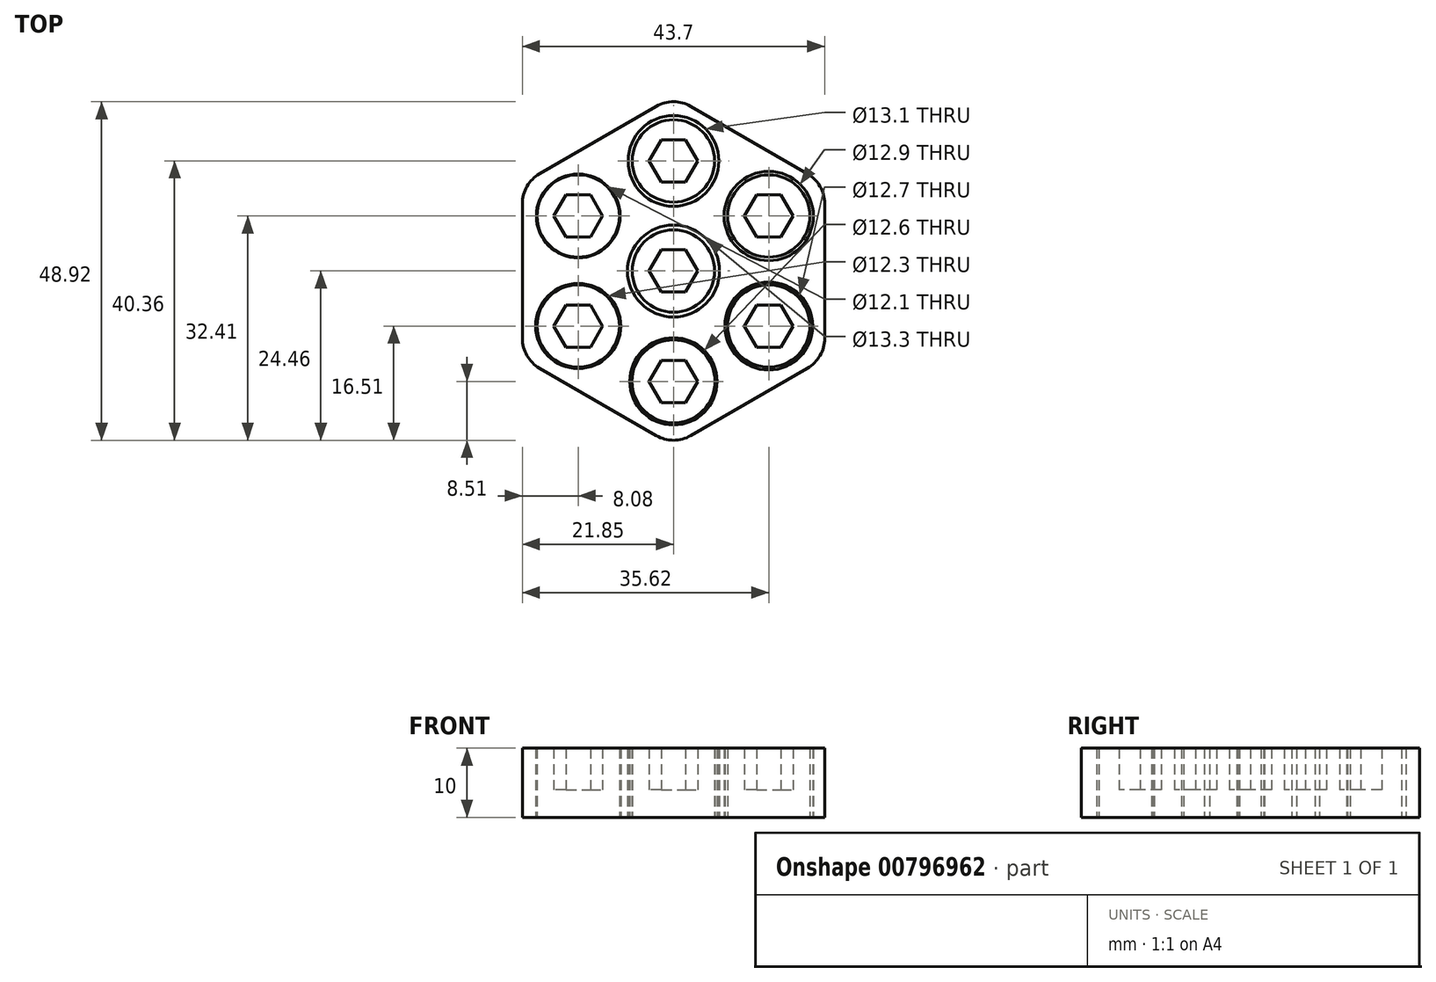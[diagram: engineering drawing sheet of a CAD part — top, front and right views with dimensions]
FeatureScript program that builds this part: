
annotation { "Feature Type Name" : "Feature", "Feature Type Description" : "" }
export const myFeature = defineFeature(function(context is Context, id is Id, definition is map)
    precondition{}
    {
        {
            assignVariable(context, id + "F0", {"name" : "z_top", "anyValue" : 10 * mm});
        }
        {
            assignVariable(context, id + "F1", {"name" : "dz_indent", "anyValue" : 6 * mm});
        }
        {
            var Q0;
            Q0=qCreatedBy(makeId("Top.planeOp"),FACE);
            var sketch = newSketch(context, id + "F2", { "sketchPlane" : qUnion([Q0])});
            skCircle(sketch, "E0.cCircle", {"center": v(0, 0) * mm, "radius": 3.05 * mm, "construction": true});
            skLineSegment(sketch, "E0.0", {"start": v(1.76, 3.05) * mm, "end": v(3.52, 0) * mm});
            skLineSegment(sketch, "E0.1", {"start": v(3.52, 0) * mm, "end": v(1.76, -3.05) * mm});
            skLineSegment(sketch, "E0.2", {"start": v(1.76, -3.05) * mm, "end": v(-1.76, -3.05) * mm});
            skLineSegment(sketch, "E0.3", {"start": v(-1.76, -3.05) * mm, "end": v(-3.52, 0) * mm});
            skLineSegment(sketch, "E0.4", {"start": v(-3.52, 0) * mm, "end": v(-1.76, 3.05) * mm});
            skLineSegment(sketch, "E0.5", {"start": v(-1.76, 3.05) * mm, "end": v(1.76, 3.05) * mm});
            skPoint(sketch, "E0.0.midPoint", {"position": v(2.64, 1.53) * mm});
            skCircle(sketch, "E1", {"center": v(0, 0) * mm, "radius": 5.95 * mm});
            skCircle(sketch, "E2.cCircle", {"center": v(0, 15.9) * mm, "radius": 3.05 * mm, "construction": true});
            skLineSegment(sketch, "E2.0", {"start": v(1.76, 18.95) * mm, "end": v(3.52, 15.9) * mm});
            skLineSegment(sketch, "E2.1", {"start": v(3.52, 15.9) * mm, "end": v(1.76, 12.85) * mm});
            skLineSegment(sketch, "E2.2", {"start": v(1.76, 12.85) * mm, "end": v(-1.76, 12.85) * mm});
            skLineSegment(sketch, "E2.3", {"start": v(-1.76, 12.85) * mm, "end": v(-3.52, 15.9) * mm});
            skLineSegment(sketch, "E2.4", {"start": v(-3.52, 15.9) * mm, "end": v(-1.76, 18.95) * mm});
            skLineSegment(sketch, "E2.5", {"start": v(-1.76, 18.95) * mm, "end": v(1.76, 18.95) * mm});
            skPoint(sketch, "E2.0.midPoint", {"position": v(2.64, 17.43) * mm});
            skCircle(sketch, "E3", {"center": v(0, 15.9) * mm, "radius": 5.95 * mm});
            skCircle(sketch, "E4.cCircle", {"center": v(0, -15.95) * mm, "radius": 3.05 * mm, "construction": true});
            skLineSegment(sketch, "E4.0", {"start": v(1.76, -12.9) * mm, "end": v(3.52, -15.95) * mm});
            skLineSegment(sketch, "E4.1", {"start": v(3.52, -15.95) * mm, "end": v(1.76, -19) * mm});
            skLineSegment(sketch, "E4.2", {"start": v(1.76, -19) * mm, "end": v(-1.76, -19) * mm});
            skLineSegment(sketch, "E4.3", {"start": v(-1.76, -19) * mm, "end": v(-3.52, -15.95) * mm});
            skLineSegment(sketch, "E4.4", {"start": v(-3.52, -15.95) * mm, "end": v(-1.76, -12.9) * mm});
            skLineSegment(sketch, "E4.5", {"start": v(-1.76, -12.9) * mm, "end": v(1.76, -12.9) * mm});
            skPoint(sketch, "E4.0.midPoint", {"position": v(2.64, -14.42) * mm});
            skCircle(sketch, "E5", {"center": v(0, -15.95) * mm, "radius": 6 * mm});
            skCircle(sketch, "E6.cCircle", {"center": v(13.77, 7.95) * mm, "radius": 3.05 * mm, "construction": true});
            skLineSegment(sketch, "E6.0", {"start": v(15.53, 11) * mm, "end": v(17.3, 7.95) * mm});
            skLineSegment(sketch, "E6.1", {"start": v(17.3, 7.95) * mm, "end": v(15.53, 4.9) * mm});
            skLineSegment(sketch, "E6.2", {"start": v(15.53, 4.9) * mm, "end": v(12, 4.9) * mm});
            skLineSegment(sketch, "E6.3", {"start": v(12, 4.9) * mm, "end": v(10.25, 7.95) * mm});
            skLineSegment(sketch, "E6.4", {"start": v(10.25, 7.95) * mm, "end": v(12, 11) * mm});
            skLineSegment(sketch, "E6.5", {"start": v(12, 11) * mm, "end": v(15.53, 11) * mm});
            skPoint(sketch, "E6.0.midPoint", {"position": v(16.41, 9.47) * mm});
            skCircle(sketch, "E7", {"center": v(13.77, 7.95) * mm, "radius": 5.95 * mm});
            skCircle(sketch, "E8.cCircle", {"center": v(13.77, -7.95) * mm, "radius": 3.05 * mm, "construction": true});
            skLineSegment(sketch, "E8.0", {"start": v(15.53, -4.9) * mm, "end": v(17.3, -7.95) * mm});
            skLineSegment(sketch, "E8.1", {"start": v(17.3, -7.95) * mm, "end": v(15.53, -11) * mm});
            skLineSegment(sketch, "E8.2", {"start": v(15.53, -11) * mm, "end": v(12, -11) * mm});
            skLineSegment(sketch, "E8.3", {"start": v(12, -11) * mm, "end": v(10.25, -7.95) * mm});
            skLineSegment(sketch, "E8.4", {"start": v(10.25, -7.95) * mm, "end": v(12, -4.9) * mm});
            skLineSegment(sketch, "E8.5", {"start": v(12, -4.9) * mm, "end": v(15.53, -4.9) * mm});
            skPoint(sketch, "E8.0.midPoint", {"position": v(16.41, -6.43) * mm});
            skCircle(sketch, "E9", {"center": v(13.77, -7.95) * mm, "radius": 5.95 * mm});
            skLineSegment(sketch, "E10", {"start": v(0, 0) * mm, "end": v(13.77, 7.95) * mm, "construction": true});
            skLineSegment(sketch, "E11", {"start": v(0, 15.9) * mm, "end": v(0, 0) * mm, "construction": true});
            skLineSegment(sketch, "E12", {"start": v(0, 0) * mm, "end": v(13.77, -7.95) * mm, "construction": true});
            skLineSegment(sketch, "E13", {"start": v(0, 0) * mm, "end": v(0, -15.95) * mm, "construction": true});
            skCircle(sketch, "E14", {"center": v(0, 0) * mm, "radius": 9.95 * mm, "construction": true});
            skCircle(sketch, "E15.cCircle", {"center": v(-13.77, -7.95) * mm, "radius": 3.05 * mm, "construction": true});
            skLineSegment(sketch, "E15.0", {"start": v(-12, -4.9) * mm, "end": v(-10.25, -7.95) * mm});
            skLineSegment(sketch, "E15.1", {"start": v(-10.25, -7.95) * mm, "end": v(-12, -11) * mm});
            skLineSegment(sketch, "E15.2", {"start": v(-12, -11) * mm, "end": v(-15.53, -11) * mm});
            skLineSegment(sketch, "E15.3", {"start": v(-15.53, -11) * mm, "end": v(-17.3, -7.95) * mm});
            skLineSegment(sketch, "E15.4", {"start": v(-17.3, -7.95) * mm, "end": v(-15.53, -4.9) * mm});
            skLineSegment(sketch, "E15.5", {"start": v(-15.53, -4.9) * mm, "end": v(-12, -4.9) * mm});
            skPoint(sketch, "E15.0.midPoint", {"position": v(-11.13, -6.43) * mm});
            skCircle(sketch, "E16", {"center": v(-13.77, -7.95) * mm, "radius": 5.95 * mm});
            skLineSegment(sketch, "E17", {"start": v(0, 0) * mm, "end": v(-13.77, -7.95) * mm, "construction": true});
            skCircle(sketch, "E18.cCircle", {"center": v(-13.77, 7.95) * mm, "radius": 3.05 * mm, "construction": true});
            skLineSegment(sketch, "E18.0", {"start": v(-12, 11) * mm, "end": v(-10.25, 7.95) * mm});
            skLineSegment(sketch, "E18.1", {"start": v(-10.25, 7.95) * mm, "end": v(-12, 4.9) * mm});
            skLineSegment(sketch, "E18.2", {"start": v(-12, 4.9) * mm, "end": v(-15.53, 4.9) * mm});
            skLineSegment(sketch, "E18.3", {"start": v(-15.53, 4.9) * mm, "end": v(-17.3, 7.95) * mm});
            skLineSegment(sketch, "E18.4", {"start": v(-17.3, 7.95) * mm, "end": v(-15.53, 11) * mm});
            skLineSegment(sketch, "E18.5", {"start": v(-15.53, 11) * mm, "end": v(-12, 11) * mm});
            skPoint(sketch, "E18.0.midPoint", {"position": v(-11.13, 9.48) * mm});
            skCircle(sketch, "E19", {"center": v(-13.77, 7.95) * mm, "radius": 5.95 * mm});
            skLineSegment(sketch, "E20", {"start": v(-13.77, 7.95) * mm, "end": v(0, 0) * mm, "construction": true});
            skCircle(sketch, "E21.cCircle", {"center": v(0, 0) * mm, "radius": 21.85 * mm, "construction": true});
            skLineSegment(sketch, "E21.0", {"start": v(21.85, 12.62) * mm, "end": v(21.85, -12.62) * mm});
            skLineSegment(sketch, "E21.1", {"start": v(21.85, -12.62) * mm, "end": v(0, -25.23) * mm});
            skLineSegment(sketch, "E21.2", {"start": v(0, -25.23) * mm, "end": v(-21.85, -12.62) * mm});
            skLineSegment(sketch, "E21.3", {"start": v(-21.85, -12.62) * mm, "end": v(-21.85, 12.62) * mm});
            skLineSegment(sketch, "E21.4", {"start": v(-21.85, 12.62) * mm, "end": v(0, 25.23) * mm});
            skLineSegment(sketch, "E21.5", {"start": v(0, 25.23) * mm, "end": v(21.85, 12.62) * mm});
            skPoint(sketch, "E21.0.midPoint", {"position": v(21.85, 0) * mm});
            skCircle(sketch, "E22", {"center": v(-13.77, 7.95) * mm, "radius": 6.05 * mm});
            skCircle(sketch, "E23", {"center": v(-13.77, -7.95) * mm, "radius": 6.15 * mm});
            skCircle(sketch, "E24", {"center": v(0, -15.95) * mm, "radius": 6.3 * mm});
            skCircle(sketch, "E25", {"center": v(13.77, -7.95) * mm, "radius": 6.35 * mm});
            skCircle(sketch, "E26", {"center": v(13.77, 7.95) * mm, "radius": 6.45 * mm});
            skCircle(sketch, "E27", {"center": v(0, 15.9) * mm, "radius": 6.55 * mm});
            skCircle(sketch, "E28", {"center": v(0, 0) * mm, "radius": 6.65 * mm});
            skSolve(sketch);
        }
        {
            var Q0;
            Q0=makeQuery(id+"F2.imprint","IMPRINT",FACE,{"disambiguationData":[TD([[makeQuery(id+"F2.imprint","IMPRINT",EDGE,{"derivedFrom":sQuery(id+"F2.wireOp",EDGE,"E21.0")}),-1.0]])]});
            extrude(context, id + "F3", {"entities" : qUnion([Q0]), "depth" : getVariable(context, 'z_top'), "offsetDistance" : 25 * mm});
        }
        {
            var Q0;
            Q0=makeQuery(id+"F3.opExtrude","SWEPT_EDGE",EDGE,{"disambiguationData":[OSD([sQuery(id+"F2.wireOp",EDGE,"E21.3"),sQuery(id+"F2.wireOp",EDGE,"E21.4")])]});
            var Q1;
            Q1=makeQuery(id+"F3.opExtrude","SWEPT_EDGE",EDGE,{"disambiguationData":[OSD([sQuery(id+"F2.wireOp",EDGE,"E21.2"),sQuery(id+"F2.wireOp",EDGE,"E21.3")])]});
            var Q2;
            Q2=makeQuery(id+"F3.opExtrude","SWEPT_EDGE",EDGE,{"disambiguationData":[OSD([sQuery(id+"F2.wireOp",EDGE,"E21.1"),sQuery(id+"F2.wireOp",EDGE,"E21.2")])]});
            var Q3;
            Q3=makeQuery(id+"F3.opExtrude","SWEPT_EDGE",EDGE,{"disambiguationData":[OSD([sQuery(id+"F2.wireOp",EDGE,"E21.4"),sQuery(id+"F2.wireOp",EDGE,"E21.5")])]});
            var Q4;
            Q4=makeQuery(id+"F3.opExtrude","SWEPT_EDGE",EDGE,{"disambiguationData":[OSD([sQuery(id+"F2.wireOp",EDGE,"E21.0"),sQuery(id+"F2.wireOp",EDGE,"E21.1")])]});
            var Q5;
            Q5=makeQuery(id+"F3.opExtrude","SWEPT_EDGE",EDGE,{"disambiguationData":[OSD([sQuery(id+"F2.wireOp",EDGE,"E21.0"),sQuery(id+"F2.wireOp",EDGE,"E21.5")])]});
            fillet(context, id + "F4", {"entities" : qUnion([Q0, Q1, Q2, Q3, Q4, Q5]), "radius" : 5 * mm, "tangentPropagation" : true, "allowEdgeOverflow" : false});
        }
        {
            var Q0;
            Q0=makeQuery(id+"F2.imprint","IMPRINT",FACE,{"disambiguationData":[TD([[makeQuery(id+"F2.imprint","IMPRINT",EDGE,{"derivedFrom":sQuery(id+"F2.wireOp",EDGE,"E18.0")}),1.0]])]});
            extrude(context, id + "F5", {"entities" : qUnion([Q0]), "depth" : getVariable(context, 'z_top'), "offsetDistance" : 25 * mm});
        }
        {
            var Q0;
            Q0=makeQuery(id+"F2.imprint","IMPRINT",FACE,{"disambiguationData":[TD([[makeQuery(id+"F2.imprint","IMPRINT",EDGE,{"derivedFrom":sQuery(id+"F2.wireOp",EDGE,"E18.0")}),-1.0]])]});
            extrude(context, id + "F6", {"entities" : qUnion([Q0]), "operationType" : NewBodyOperationType.ADD, "depth" : getVariable(context, 'z_top') - getVariable(context, 'dz_indent'), "offsetDistance" : 25 * mm});
        }
        {
            var Q0;
            Q0=makeQuery(id+"F2.imprint","IMPRINT",FACE,{"disambiguationData":[TD([[makeQuery(id+"F2.imprint","IMPRINT",EDGE,{"derivedFrom":sQuery(id+"F2.wireOp",EDGE,"E15.0")}),1.0]])]});
            extrude(context, id + "F7", {"entities" : qUnion([Q0]), "depth" : getVariable(context, 'z_top'), "offsetDistance" : 25 * mm});
        }
        {
            var Q0;
            Q0=makeQuery(id+"F2.imprint","IMPRINT",FACE,{"disambiguationData":[TD([[makeQuery(id+"F2.imprint","IMPRINT",EDGE,{"derivedFrom":sQuery(id+"F2.wireOp",EDGE,"E15.0")}),-1.0]])]});
            extrude(context, id + "F8", {"entities" : qUnion([Q0]), "operationType" : NewBodyOperationType.ADD, "depth" : getVariable(context, 'z_top') - getVariable(context, 'dz_indent'), "offsetDistance" : 25 * mm});
        }
        {
            var Q0;
            Q0=makeQuery(id+"F2.imprint","IMPRINT",FACE,{"disambiguationData":[TD([[makeQuery(id+"F2.imprint","IMPRINT",EDGE,{"derivedFrom":sQuery(id+"F2.wireOp",EDGE,"E4.0")}),1.0]])]});
            extrude(context, id + "F9", {"entities" : qUnion([Q0]), "depth" : getVariable(context, 'z_top'), "offsetDistance" : 25 * mm});
        }
        {
            var Q0;
            Q0=makeQuery(id+"F2.imprint","IMPRINT",FACE,{"disambiguationData":[TD([[makeQuery(id+"F2.imprint","IMPRINT",EDGE,{"derivedFrom":sQuery(id+"F2.wireOp",EDGE,"E4.0")}),-1.0]])]});
            extrude(context, id + "F10", {"entities" : qUnion([Q0]), "operationType" : NewBodyOperationType.ADD, "depth" : getVariable(context, 'z_top') - getVariable(context, 'dz_indent'), "offsetDistance" : 25 * mm});
        }
        {
            var Q0;
            Q0=makeQuery(id+"F2.imprint","IMPRINT",FACE,{"disambiguationData":[TD([[makeQuery(id+"F2.imprint","IMPRINT",EDGE,{"derivedFrom":sQuery(id+"F2.wireOp",EDGE,"E8.0")}),1.0]])]});
            extrude(context, id + "F11", {"entities" : qUnion([Q0]), "depth" : getVariable(context, 'z_top'), "offsetDistance" : 25 * mm});
        }
        {
            var Q0;
            Q0=makeQuery(id+"F2.imprint","IMPRINT",FACE,{"disambiguationData":[TD([[makeQuery(id+"F2.imprint","IMPRINT",EDGE,{"derivedFrom":sQuery(id+"F2.wireOp",EDGE,"E8.0")}),-1.0]])]});
            extrude(context, id + "F12", {"entities" : qUnion([Q0]), "operationType" : NewBodyOperationType.ADD, "depth" : getVariable(context, 'z_top') - getVariable(context, 'dz_indent'), "offsetDistance" : 25 * mm});
        }
        {
            var Q0;
            Q0=makeQuery(id+"F2.imprint","IMPRINT",FACE,{"disambiguationData":[TD([[makeQuery(id+"F2.imprint","IMPRINT",EDGE,{"derivedFrom":sQuery(id+"F2.wireOp",EDGE,"E6.0")}),1.0]])]});
            extrude(context, id + "F13", {"entities" : qUnion([Q0]), "depth" : getVariable(context, 'z_top'), "offsetDistance" : 25 * mm});
        }
        {
            var Q0;
            Q0=makeQuery(id+"F2.imprint","IMPRINT",FACE,{"disambiguationData":[TD([[makeQuery(id+"F2.imprint","IMPRINT",EDGE,{"derivedFrom":sQuery(id+"F2.wireOp",EDGE,"E6.0")}),-1.0]])]});
            extrude(context, id + "F14", {"entities" : qUnion([Q0]), "operationType" : NewBodyOperationType.ADD, "depth" : getVariable(context, 'z_top') - getVariable(context, 'dz_indent'), "offsetDistance" : 25 * mm});
        }
        {
            var Q0;
            Q0=makeQuery(id+"F2.imprint","IMPRINT",FACE,{"disambiguationData":[TD([[makeQuery(id+"F2.imprint","IMPRINT",EDGE,{"derivedFrom":sQuery(id+"F2.wireOp",EDGE,"E2.0")}),1.0]])]});
            extrude(context, id + "F15", {"entities" : qUnion([Q0]), "depth" : getVariable(context, 'z_top'), "offsetDistance" : 25 * mm});
        }
        {
            var Q0;
            Q0=makeQuery(id+"F2.imprint","IMPRINT",FACE,{"disambiguationData":[TD([[makeQuery(id+"F2.imprint","IMPRINT",EDGE,{"derivedFrom":sQuery(id+"F2.wireOp",EDGE,"E2.0")}),-1.0]])]});
            extrude(context, id + "F16", {"entities" : qUnion([Q0]), "operationType" : NewBodyOperationType.ADD, "depth" : getVariable(context, 'z_top') - getVariable(context, 'dz_indent'), "offsetDistance" : 25 * mm});
        }
        {
            var Q0;
            Q0=makeQuery(id+"F2.imprint","IMPRINT",FACE,{"disambiguationData":[TD([[makeQuery(id+"F2.imprint","IMPRINT",EDGE,{"derivedFrom":sQuery(id+"F2.wireOp",EDGE,"E0.0")}),1.0]])]});
            extrude(context, id + "F17", {"entities" : qUnion([Q0]), "depth" : getVariable(context, 'z_top'), "offsetDistance" : 25 * mm});
        }
        {
            var Q0;
            Q0=makeQuery(id+"F2.imprint","IMPRINT",FACE,{"disambiguationData":[TD([[makeQuery(id+"F2.imprint","IMPRINT",EDGE,{"derivedFrom":sQuery(id+"F2.wireOp",EDGE,"E0.0")}),-1.0]])]});
            extrude(context, id + "F18", {"entities" : qUnion([Q0]), "operationType" : NewBodyOperationType.ADD, "depth" : getVariable(context, 'z_top') - getVariable(context, 'dz_indent'), "offsetDistance" : 25 * mm});
        }
    });
